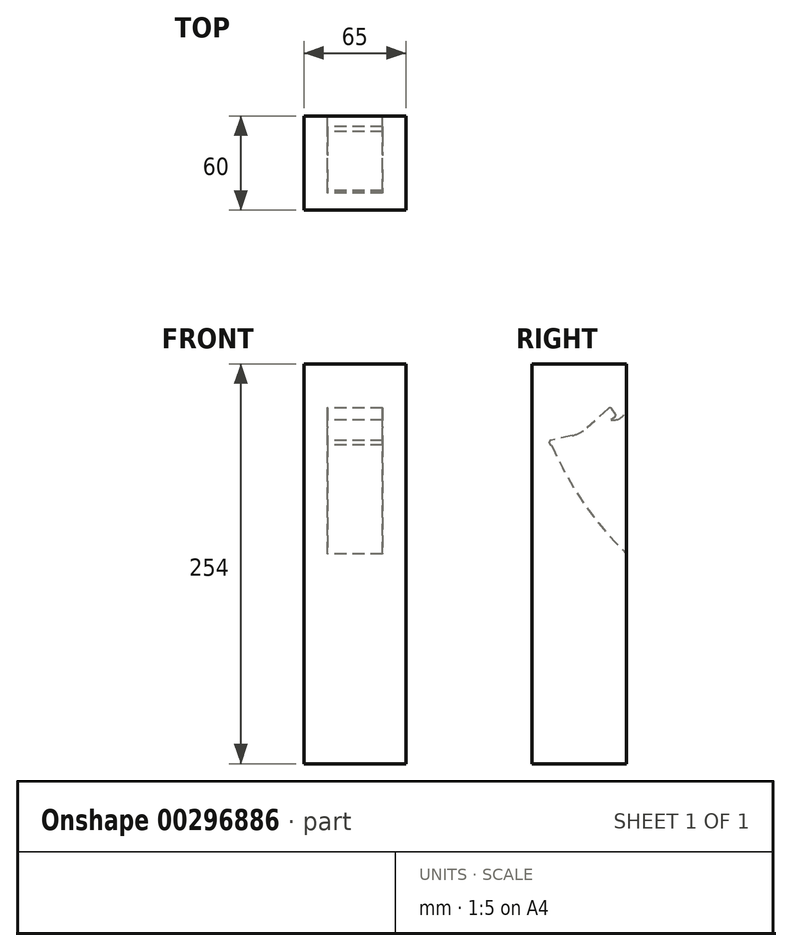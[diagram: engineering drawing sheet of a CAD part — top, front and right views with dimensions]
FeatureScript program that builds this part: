
annotation { "Feature Type Name" : "Feature", "Feature Type Description" : "" }
export const myFeature = defineFeature(function(context is Context, id is Id, definition is map)
    precondition{}
    {
        {
            var Q0;
            Q0=qCreatedBy(makeId("Right.planeOp"),FACE);
            var sketch = newSketch(context, id + "F0", { "sketchPlane" : qUnion([Q0])});
            skLineSegment(sketch, "E0", {"start": v(0, 0) * mm, "end": v(0, 254) * mm});
            skLineSegment(sketch, "E1", {"start": v(0, 254) * mm, "end": v(60, 254) * mm});
            skLineSegment(sketch, "E2", {"start": v(60, 0) * mm, "end": v(0, 0) * mm});
            skLineSegment(sketch, "E3", {"start": v(60, 254) * mm, "end": v(60, 226.39) * mm});
            skLineSegment(sketch, "E4", {"start": v(60, 0) * mm, "end": v(60, 133.36) * mm});
            skLineSegment(sketch, "E5", {"start": v(52.42, 220) * mm, "end": v(50, 218.39) * mm});
            skLineSegment(sketch, "E6", {"start": v(50, 218.39) * mm, "end": v(52, 218.39) * mm});
            skPoint(sketch, "E7.visualSharp", {"position": v(60, 218.39) * mm});
            skArc(sketch, "E7.filletArc", {"start": v(52, 218.39) * mm, "mid": v(57.66, 220.73) * mm, "end": v(60, 226.39) * mm});
            skLineSegment(sketch, "E8", {"start": v(52.85, 222.21) * mm, "end": v(50.8, 225.27) * mm});
            skPoint(sketch, "E9.visualSharp", {"position": v(60, 202.42) * mm});
            skPoint(sketch, "E10.visualSharp", {"position": v(53.74, 220.9) * mm});
            skArc(sketch, "E10.filletArc", {"start": v(52.42, 220) * mm, "mid": v(53.09, 221.02) * mm, "end": v(52.85, 222.21) * mm});
            skPoint(sketch, "E11.visualSharp", {"position": v(49.55, 227.12) * mm});
            skArc(sketch, "E11.filletArc", {"start": v(50.8, 225.27) * mm, "mid": v(49.67, 225.97) * mm, "end": v(48.4, 225.56) * mm});
            skPoint(sketch, "E12.visualSharp", {"position": v(15.59, 202.42) * mm});
            skArc(sketch, "E12.filletArc", {"start": v(11.55, 205.33) * mm, "mid": v(10.91, 203.55) * mm, "end": v(12.43, 202.42) * mm});
            skLineSegment(sketch, "E13", {"start": v(48.4, 225.56) * mm, "end": v(34.9, 213.22) * mm});
            skLineSegment(sketch, "E14", {"start": v(25.72, 208.45) * mm, "end": v(11.55, 205.33) * mm});
            skPoint(sketch, "E15.visualSharp", {"position": v(30.95, 209.6) * mm});
            skArc(sketch, "E15.filletArc", {"start": v(25.72, 208.45) * mm, "mid": v(30.63, 210.23) * mm, "end": v(34.9, 213.22) * mm});
            skArc(sketch, "E16", {"start": v(12.43, 202.42) * mm, "mid": v(32.8, 165.54) * mm, "end": v(60, 133.36) * mm});
            skSolve(sketch);
        }
        {
            var Q0;
            Q0=makeQuery(id+"F0.imprint","IMPRINT",FACE,{"disambiguationData":[TD([[makeQuery(id+"F0.imprint","IMPRINT",EDGE,{"derivedFrom":sQuery(id+"F0.wireOp",EDGE,"E0")}),-1.0]])]});
            extrude(context, id + "F1", {"entities" : qUnion([Q0]), "depth" : 35 * mm});
        }
        {
            var Q0;
            Q0=makeQuery(id+"F1.opExtrude","SWEPT_FACE",FACE,{"disambiguationData":[OSD([sQuery(id+"F0.wireOp",EDGE,"E0")])]});
            var sketch = newSketch(context, id + "F2", { "sketchPlane" : qUnion([Q0])});
            skLineSegment(sketch, "E17.bottom", {"start": v(0, 254) * mm, "end": v(-15, 254) * mm});
            skLineSegment(sketch, "E17.top", {"start": v(0, 0) * mm, "end": v(-15, 0) * mm});
            skLineSegment(sketch, "E17.left", {"start": v(0, 254) * mm, "end": v(0, 0) * mm});
            skLineSegment(sketch, "E17.right", {"start": v(-15, 254) * mm, "end": v(-15, 0) * mm});
            skLineSegment(sketch, "E18.bottom", {"start": v(35, 254) * mm, "end": v(50, 254) * mm});
            skLineSegment(sketch, "E18.top", {"start": v(35, 0) * mm, "end": v(50, 0) * mm});
            skLineSegment(sketch, "E18.left", {"start": v(35, 254) * mm, "end": v(35, 0) * mm});
            skLineSegment(sketch, "E18.right", {"start": v(50, 254) * mm, "end": v(50, 0) * mm});
            skSolve(sketch);
        }
        {
            var Q0;
            Q0=makeQuery(id+"F2.imprint","IMPRINT",FACE,{"disambiguationData":[TD([[makeQuery(id+"F2.imprint","IMPRINT",EDGE,{"derivedFrom":sQuery(id+"F2.wireOp",EDGE,"E17.bottom")}),1.0]])]});
            var Q1;
            Q1=makeQuery(id+"F2.imprint","IMPRINT",FACE,{"disambiguationData":[TD([[makeQuery(id+"F2.imprint","IMPRINT",EDGE,{"derivedFrom":sQuery(id+"F2.wireOp",EDGE,"E18.bottom")}),-1.0]])]});
            extrude(context, id + "F3", {"entities" : qUnion([Q0, Q1]), "operationType" : NewBodyOperationType.ADD, "oppositeDirection" : true, "depth" : 60 * mm});
        }
    });
